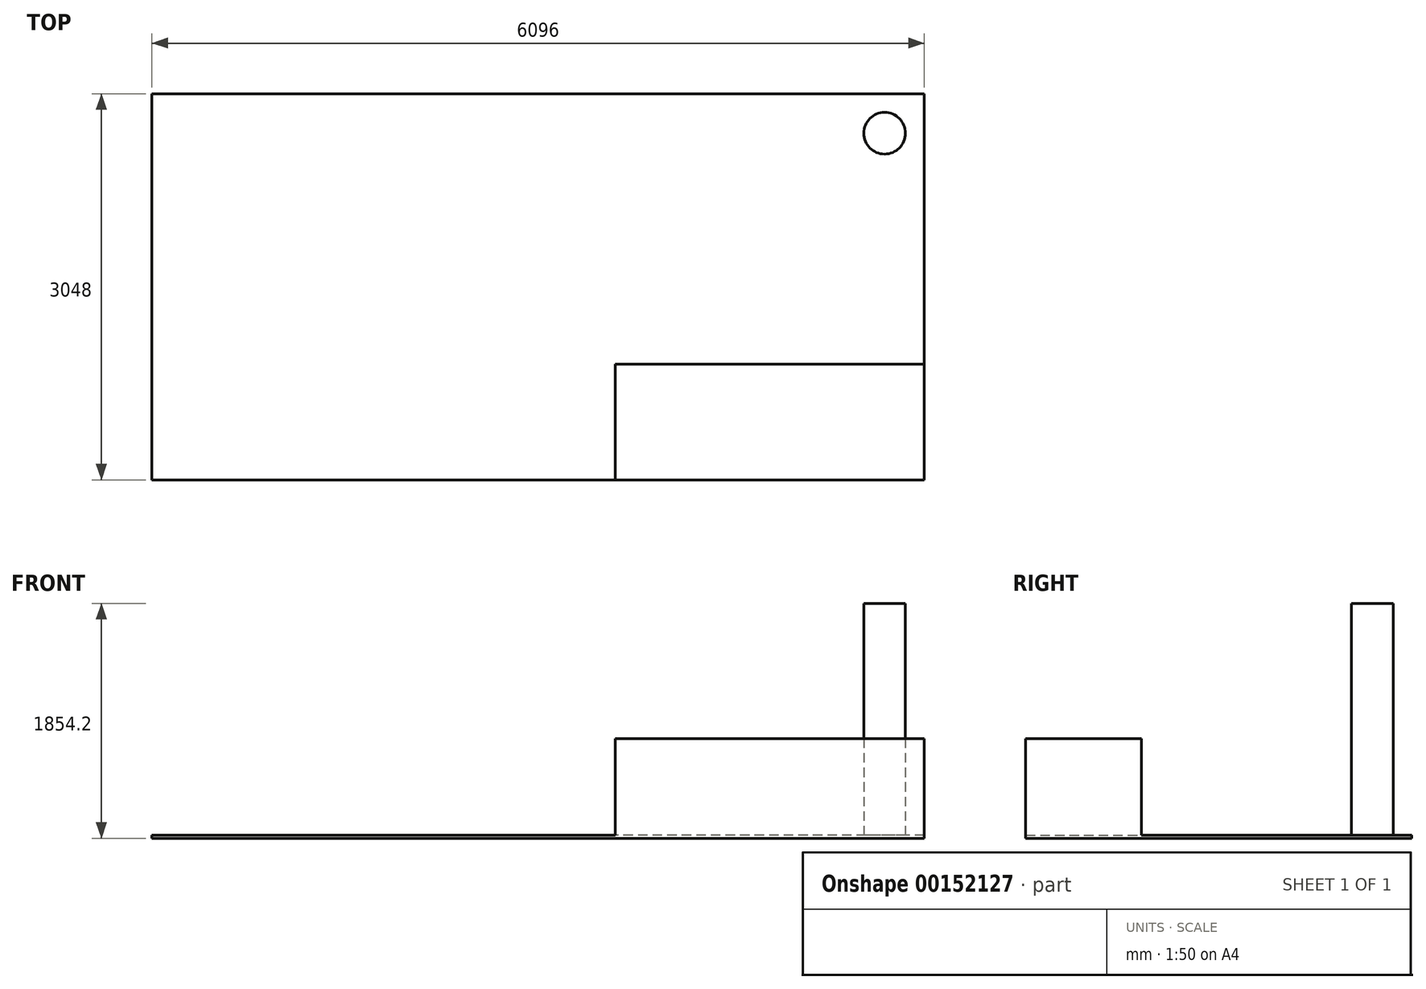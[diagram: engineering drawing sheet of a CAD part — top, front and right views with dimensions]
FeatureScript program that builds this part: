
annotation { "Feature Type Name" : "Feature", "Feature Type Description" : "" }
export const myFeature = defineFeature(function(context is Context, id is Id, definition is map)
    precondition{}
    {
        {
            var Q0;
            Q0=qCreatedBy(makeId("Top.planeOp"),FACE);
            var sketch = newSketch(context, id + "F0", { "sketchPlane" : qUnion([Q0])});
            skLineSegment(sketch, "E0.bottom", {"start": v(3048, 1524) * mm, "end": v(-3048, 1524) * mm});
            skLineSegment(sketch, "E0.top", {"start": v(3048, -1524) * mm, "end": v(-3048, -1524) * mm});
            skLineSegment(sketch, "E0.left", {"start": v(3048, 1524) * mm, "end": v(3048, -1524) * mm});
            skLineSegment(sketch, "E0.right", {"start": v(-3048, 1524) * mm, "end": v(-3048, -1524) * mm});
            skPoint(sketch, "E0.middle", {"position": v(0, 0) * mm});
            skSolve(sketch);
        }
        {
            var Q0;
            Q0 = qSketchRegion(id + "F0", true);
            extrude(context, id + "F1", {"entities" : qUnion([Q0]), "oppositeDirection" : true, "depth" : 25.4 * mm});
        }
        {
            var Q0;
            Q0=makeQuery(id+"F1.opExtrude","CAP_FACE",FACE,{"disambiguationData":[OSD([sQuery(id+"F0.wireOp",EDGE,"E0.bottom"),sQuery(id+"F0.wireOp",EDGE,"E0.top"),sQuery(id+"F0.wireOp",EDGE,"E0.left"),sQuery(id+"F0.wireOp",EDGE,"E0.right")])],"isStart":true});
            var sketch = newSketch(context, id + "F2", { "sketchPlane" : qUnion([Q0])});
            skLineSegment(sketch, "E1.bottom", {"start": v(3048, -1524) * mm, "end": v(609.6, -1524) * mm});
            skLineSegment(sketch, "E1.top", {"start": v(3048, -609.6) * mm, "end": v(609.6, -609.6) * mm});
            skLineSegment(sketch, "E1.left", {"start": v(3048, -1524) * mm, "end": v(3048, -609.6) * mm});
            skLineSegment(sketch, "E1.right", {"start": v(609.6, -1524) * mm, "end": v(609.6, -609.6) * mm});
            skSolve(sketch);
        }
        {
            var Q0;
            Q0 = qSketchRegion(id + "F2", true);
            extrude(context, id + "F3", {"entities" : qUnion([Q0]), "operationType" : NewBodyOperationType.ADD, "depth" : 762 * mm});
        }
        {
            var Q0;
            Q0=makeQuery(id+"F1.opExtrude","CAP_FACE",FACE,{"disambiguationData":[OSD([sQuery(id+"F0.wireOp",EDGE,"E0.bottom"),sQuery(id+"F0.wireOp",EDGE,"E0.top"),sQuery(id+"F0.wireOp",EDGE,"E0.left"),sQuery(id+"F0.wireOp",EDGE,"E0.right")])],"isStart":true});
            var sketch = newSketch(context, id + "F4", { "sketchPlane" : qUnion([Q0])});
            skCircle(sketch, "E2", {"center": v(2733.94, 1211.6) * mm, "radius": 164.39 * mm});
            skSolve(sketch);
        }
        {
            var Q0;
            Q0 = qSketchRegion(id + "F4", true);
            extrude(context, id + "F5", {"entities" : qUnion([Q0]), "operationType" : NewBodyOperationType.ADD, "depth" : 1828.8 * mm});
        }
    });
